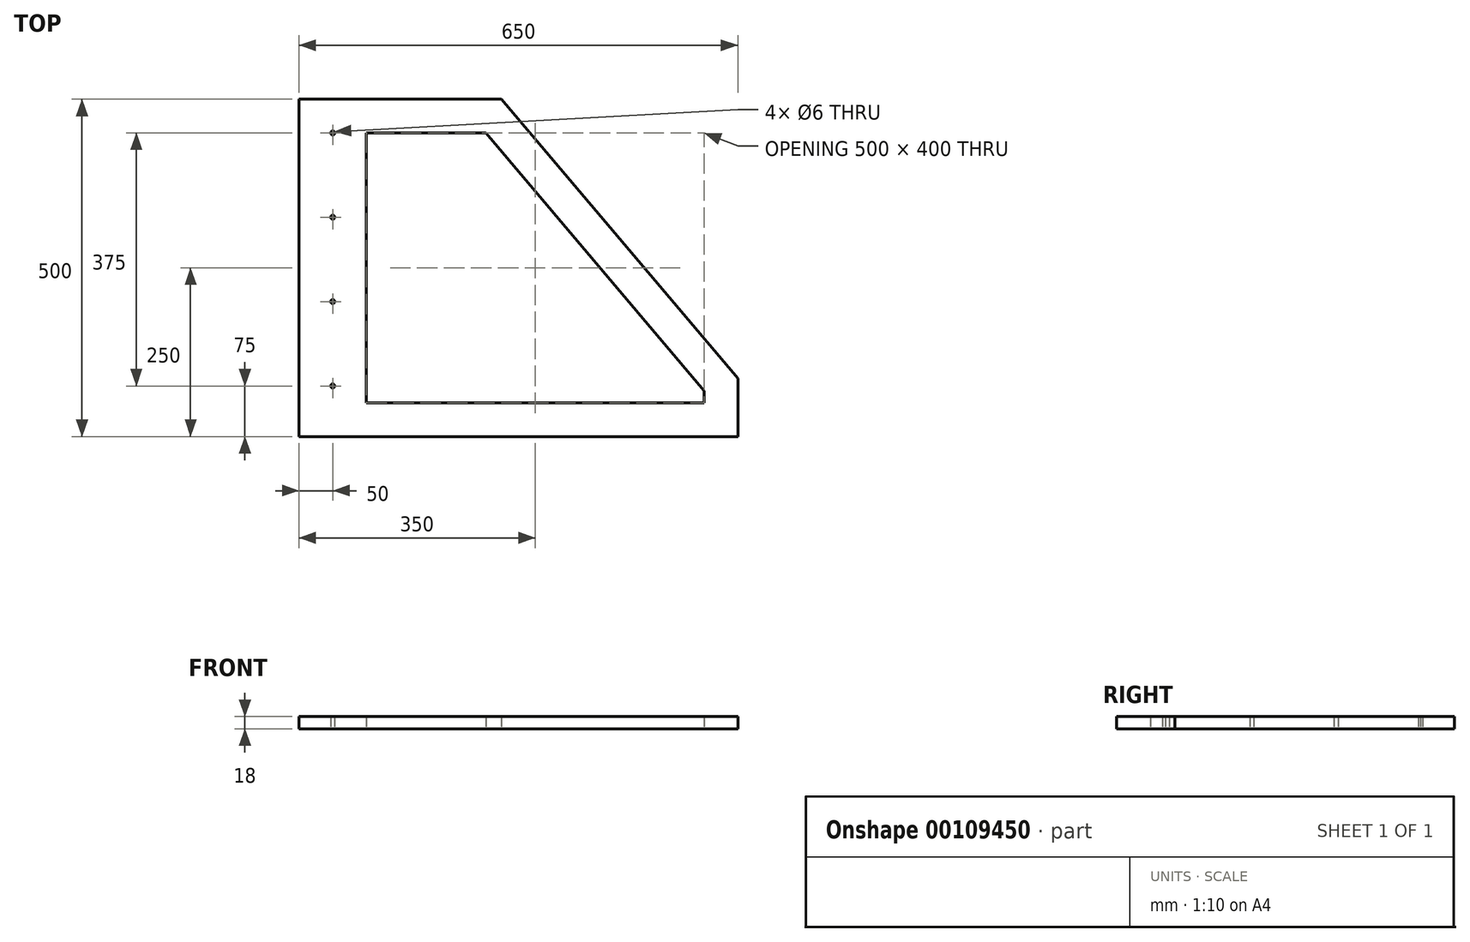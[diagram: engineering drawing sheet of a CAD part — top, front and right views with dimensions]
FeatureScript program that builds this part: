
annotation { "Feature Type Name" : "Feature", "Feature Type Description" : "" }
export const myFeature = defineFeature(function(context is Context, id is Id, definition is map)
    precondition{}
    {
        {
            var Q0;
            Q0=qCreatedBy(makeId("Top.planeOp"),FACE);
            var sketch = newSketch(context, id + "F0", { "sketchPlane" : qUnion([Q0])});
            skPoint(sketch, "E0.middle", {"position": v(0, 0) * mm});
            skLineSegment(sketch, "E1", {"start": v(0, 0) * mm, "end": v(550, 0) * mm});
            skLineSegment(sketch, "E2", {"start": v(550, 0) * mm, "end": v(550, 86.31) * mm});
            skLineSegment(sketch, "E3", {"start": v(550, 86.31) * mm, "end": v(200, 500) * mm});
            skLineSegment(sketch, "E4", {"start": v(200, 500) * mm, "end": v(0, 500) * mm});
            skLineSegment(sketch, "E5", {"start": v(0, 500) * mm, "end": v(0, 0) * mm});
            skLineSegment(sketch, "E6", {"start": v(0, 500) * mm, "end": v(-100, 500) * mm});
            skLineSegment(sketch, "E7", {"start": v(-100, 500) * mm, "end": v(-100, 0) * mm});
            skLineSegment(sketch, "E8", {"start": v(-100, 0) * mm, "end": v(0, 0) * mm});
            skLineSegment(sketch, "E9.1", {"start": v(500, 68) * mm, "end": v(176.8, 450) * mm});
            skLineSegment(sketch, "E9.4", {"start": v(500, 50) * mm, "end": v(500, 68) * mm});
            skLineSegment(sketch, "E10", {"start": v(500, 50) * mm, "end": v(0, 50) * mm});
            skLineSegment(sketch, "E11", {"start": v(176.8, 450) * mm, "end": v(0, 450) * mm});
            skLineSegment(sketch, "E12", {"start": v(-50, 500) * mm, "end": v(-50, 0) * mm});
            skCircle(sketch, "E13", {"center": v(-50, 450) * mm, "radius": 3 * mm});
            skCircle(sketch, "E14.0.1.0", {"center": v(-50, 325) * mm, "radius": 3 * mm});
            skCircle(sketch, "E14.0.2.0", {"center": v(-50, 200) * mm, "radius": 3 * mm});
            skCircle(sketch, "E14.0.3.0", {"center": v(-50, 75) * mm, "radius": 3 * mm});
            skLineSegment(sketch, "E14.direction2", {"start": v(-50, 450) * mm, "end": v(-50, 325) * mm, "construction": true});
            skSolve(sketch);
        }
        {
            var Q0;
            {var subQ1=sQuery(id+"F0.wireOp",EDGE,"E1");Q0=makeQuery(id+"F0.imprint","IMPRINT",FACE,{"disambiguationData":[TD([[makeQuery(id+"F0.imprint","IMPRINT",EDGE,{"derivedFrom":subQ1}),1.0]])]});}
            var Q1;
            {var subQ9=sQuery(id+"F0.wireOp",EDGE,"E5");var subQ20=makeQuery(id+"F0.imprint","INTERSECT",VERTEX,{"derivedFrom":[subQ9,sQuery(id+"F0.wireOp",EDGE,"E10")]});Q1=makeQuery(id+"F0.imprint","IMPRINT",FACE,{"disambiguationData":[TD([[makeQuery(id+"F0.imprint","IMPRINT",EDGE,{"disambiguationData":[TD([[subQ20,1.0]])],"derivedFrom":subQ9}),-1.0]])]});}
            var Q2;
            {var subQ13=sQuery(id+"F0.wireOp",EDGE,"E7");Q2=makeQuery(id+"F0.imprint","IMPRINT",FACE,{"disambiguationData":[TD([[makeQuery(id+"F0.imprint","IMPRINT",EDGE,{"derivedFrom":subQ13}),1.0]])]});}
            extrude(context, id + "F1", {"entities" : qUnion([Q0, Q1, Q2]), "depth" : 18 * mm});
        }
    });
